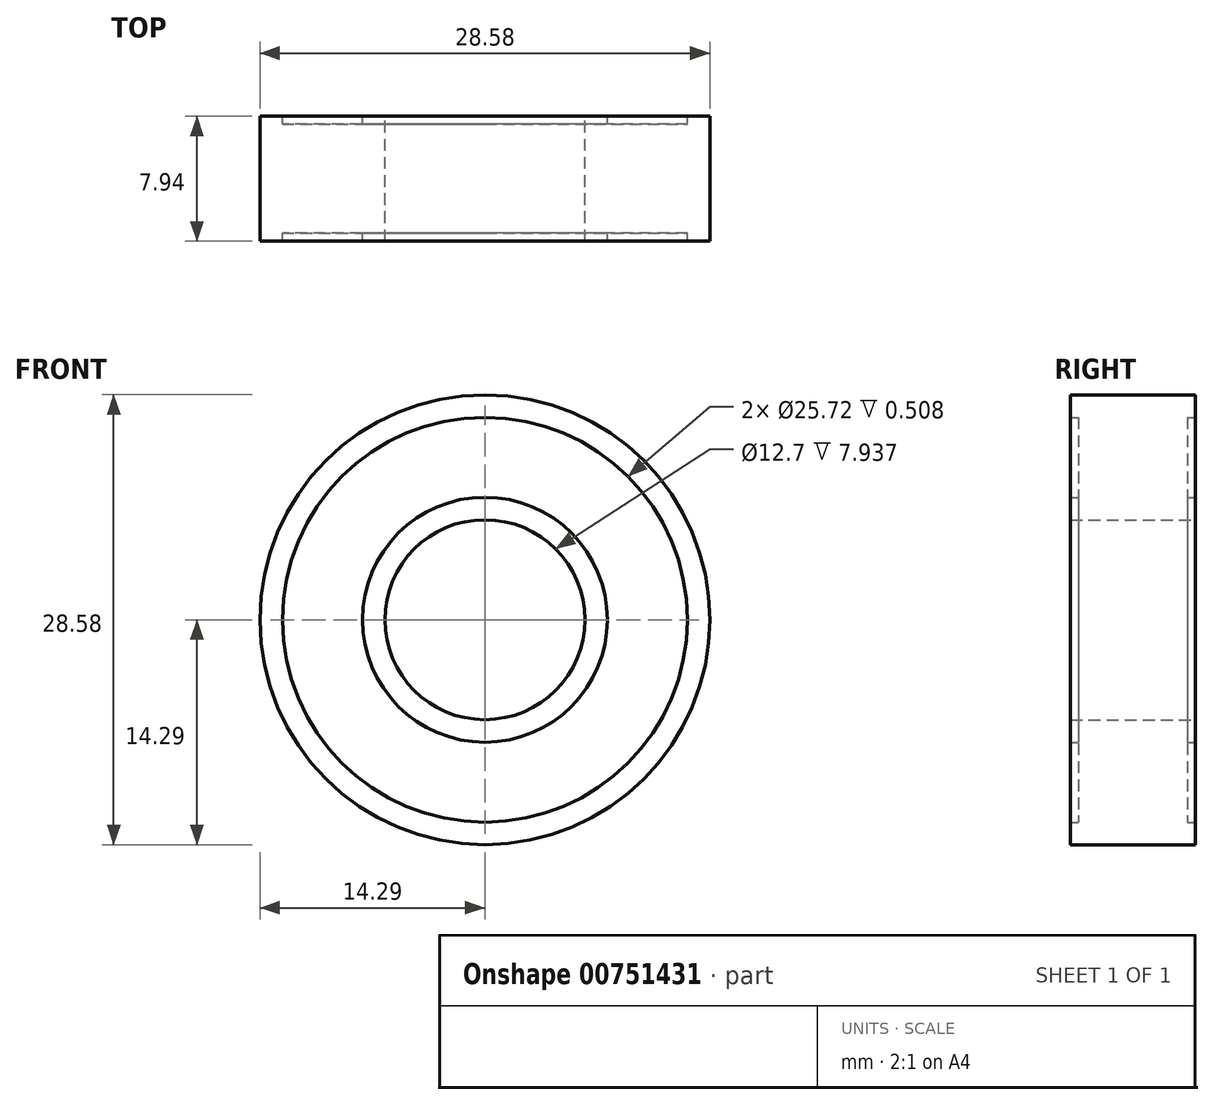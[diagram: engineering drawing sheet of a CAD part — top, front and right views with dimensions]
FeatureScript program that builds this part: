
annotation { "Feature Type Name" : "Feature", "Feature Type Description" : "" }
export const myFeature = defineFeature(function(context is Context, id is Id, definition is map)
    precondition{}
    {
        {
            var Q0;
            Q0=qCreatedBy(makeId("Top.planeOp"),FACE);
            var sketch = newSketch(context, id + "F0", { "sketchPlane" : qUnion([Q0])});
            skLineSegment(sketch, "E0.bottom", {"start": v(6.35, 3.97) * mm, "end": v(14.29, 3.97) * mm});
            skLineSegment(sketch, "E0.top", {"start": v(6.35, -3.97) * mm, "end": v(14.29, -3.97) * mm});
            skLineSegment(sketch, "E0.left", {"start": v(6.35, 3.97) * mm, "end": v(6.35, -3.97) * mm});
            skLineSegment(sketch, "E0.right", {"start": v(14.29, 3.97) * mm, "end": v(14.29, -3.97) * mm});
            skLineSegment(sketch, "E1", {"start": v(0, 59.5) * mm, "end": v(0, -47.6) * mm, "construction": true});
            skLineSegment(sketch, "E2.bottom", {"start": v(7.78, 3.97) * mm, "end": v(12.86, 3.97) * mm});
            skLineSegment(sketch, "E2.top", {"start": v(7.78, 3.46) * mm, "end": v(12.86, 3.46) * mm});
            skLineSegment(sketch, "E2.left", {"start": v(7.78, 3.97) * mm, "end": v(7.78, 3.46) * mm});
            skLineSegment(sketch, "E2.right", {"start": v(12.86, 3.97) * mm, "end": v(12.86, 3.46) * mm});
            skLineSegment(sketch, "E3.bottom", {"start": v(12.86, -3.97) * mm, "end": v(7.78, -3.97) * mm});
            skLineSegment(sketch, "E3.top", {"start": v(12.86, -3.46) * mm, "end": v(7.78, -3.46) * mm});
            skLineSegment(sketch, "E3.left", {"start": v(12.86, -3.97) * mm, "end": v(12.86, -3.46) * mm});
            skLineSegment(sketch, "E3.right", {"start": v(7.78, -3.97) * mm, "end": v(7.78, -3.46) * mm});
            skPoint(sketch, "E4", {"position": v(10.32, 3.97) * mm});
            skPoint(sketch, "E5", {"position": v(10.32, -3.97) * mm});
            skSolve(sketch);
        }
        {
            var Q0;
            Q0=makeQuery(id+"F0.imprint","IMPRINT",FACE,{"disambiguationData":[TD([[makeQuery(id+"F0.imprint","IMPRINT",EDGE,{"derivedFrom":sQuery(id+"F0.wireOp",EDGE,"E0.bottom")}),-1.0]])]});
            var Q1;
            Q1=sQuery(id+"F0.wireOp",EDGE,"E1");
            revolve(context, id + "F1", {"surfaceOperationType" : NewSurfaceOperationType.NEW, "entities" : qUnion([Q0]), "axis" : qUnion([Q1]), "revolveType" : RevolveType.FULL});
        }
    });
